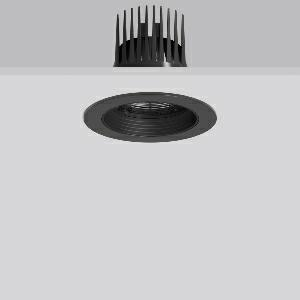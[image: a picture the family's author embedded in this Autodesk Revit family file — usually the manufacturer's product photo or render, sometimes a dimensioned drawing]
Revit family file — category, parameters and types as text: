
# Revit family: heledon_maxi_e_901762_003_2_d940
name_source: partatom
category: Lighting Fixtures
units: mm (PartAtom-declared; Revit-internal decimal feet)

## family parameters
Cut with Voids When Loaded = No
Host = Face
Light Source = No
Part Type = Normal
Room Calculation Point = No
Round Connector Dimension = Use Diameter
Shared = No

## types (1)
- HELEDON maxi E (1 x LED Modul 927, 2650 lm, 2700)
    Apparent Load = 25 VA
    Approval mark = CE
    CIE Flux Codes = 96 100 100 100 100
    Color Rendering = 92
    Color Temperature = 2700
    Default Elevation = 1800 mm
    Description = Series: HELEDON maxi
Round recessed downlight. Housing: die-cast aluminium, powder-coated. Black plastic ring and recessed LED to prevent glare from the side. Optical assembly with lens made of plastic (polycarbonate) for the best homogeneous light distribution - can be changed without tools. Best colour rendering index Ra>90. Suitable for Recessed ceiling mounting. Installation without tools thanks to spring fastening system. Including separate LED converter with connecting cable 600 mm.High quality converter without flickering and stroboscopic effect. Through-wiring box (5 pole) available as accessory. The following accessories can be mounted without use of tools: interchangeable lenses, decorative glasses, honeycomb louvre, clear and frosted diffusers, white interchangeable plastic ring. 
Colour: deep black, matt (RAL 9005)
Diameter: 162 mm
Height: 3 mm
Cut-out diameter: 152 mm
Recess height: 200 mm
Luminaire: recess height: 135 mm
Lamp: LED
Socket: without socket
Colour temperature: 2700K
Colour rendering index (CRI): 92
System power: 25 W
Rated luminous flux: 2650 lm
Luminous efficiency: 106 lm/W
Control gear: Regulated power supply
Protection class: II
Type of protection: IP 20
    Height = 0 mm  [stored 0 ft]
    Lamp = 1 x LED Modul 927
    Lamp Light Flux = 2650 lm
    Lamp count = 1
    Length = 162 mm
    Lifetime = 50000 h
    Luminous efficacy = 106 lm/W
    Manufacturer = RZB
    ModVariant = No
    Model = 901762.003.2
    Mounting Place = Ceiling
    Mounting Type = Recessed
    Number of Poles = 1
    OnlyDefault = Yes
    Power Factor = 1
    Product Name = HELEDON maxi E
    Product group = Recessed downlights
    ProductGroupID = 402
    Protection Class = Protection class II
    Protection Degree = IP 20
    RLX_Detail_Level = 1
    RLX_Emergency_Light_Flux = 0 lm
    RLX_Emergency_Type = 0
    RLX_Emergency_Type_DB = No
    RlxData = <blob elided: 120673 chars, md5=9cbcd126>
    Socket = socket
    Standby Power = 0 W
    System Light Flux = 2650 lm
    System Power = 25 W
    Type Comments = Product without accessories
    Type Image = 901663.003.jpg
    URL = http://relux.com
    VarID = ---
    Voltage = 230 V
    Voltage Range = 220-240 V
    Weight = 0.00 kg
    Width = 0 mm  [stored 0 ft]

note: [stored X ft] marks values corroborated as IEEE doubles in the binary element streams (Revit-internal decimal feet)

## geometry (parser evidence)
native form markers: Blend x4, Sweep x10
no freeform markers — native parametric forms only
